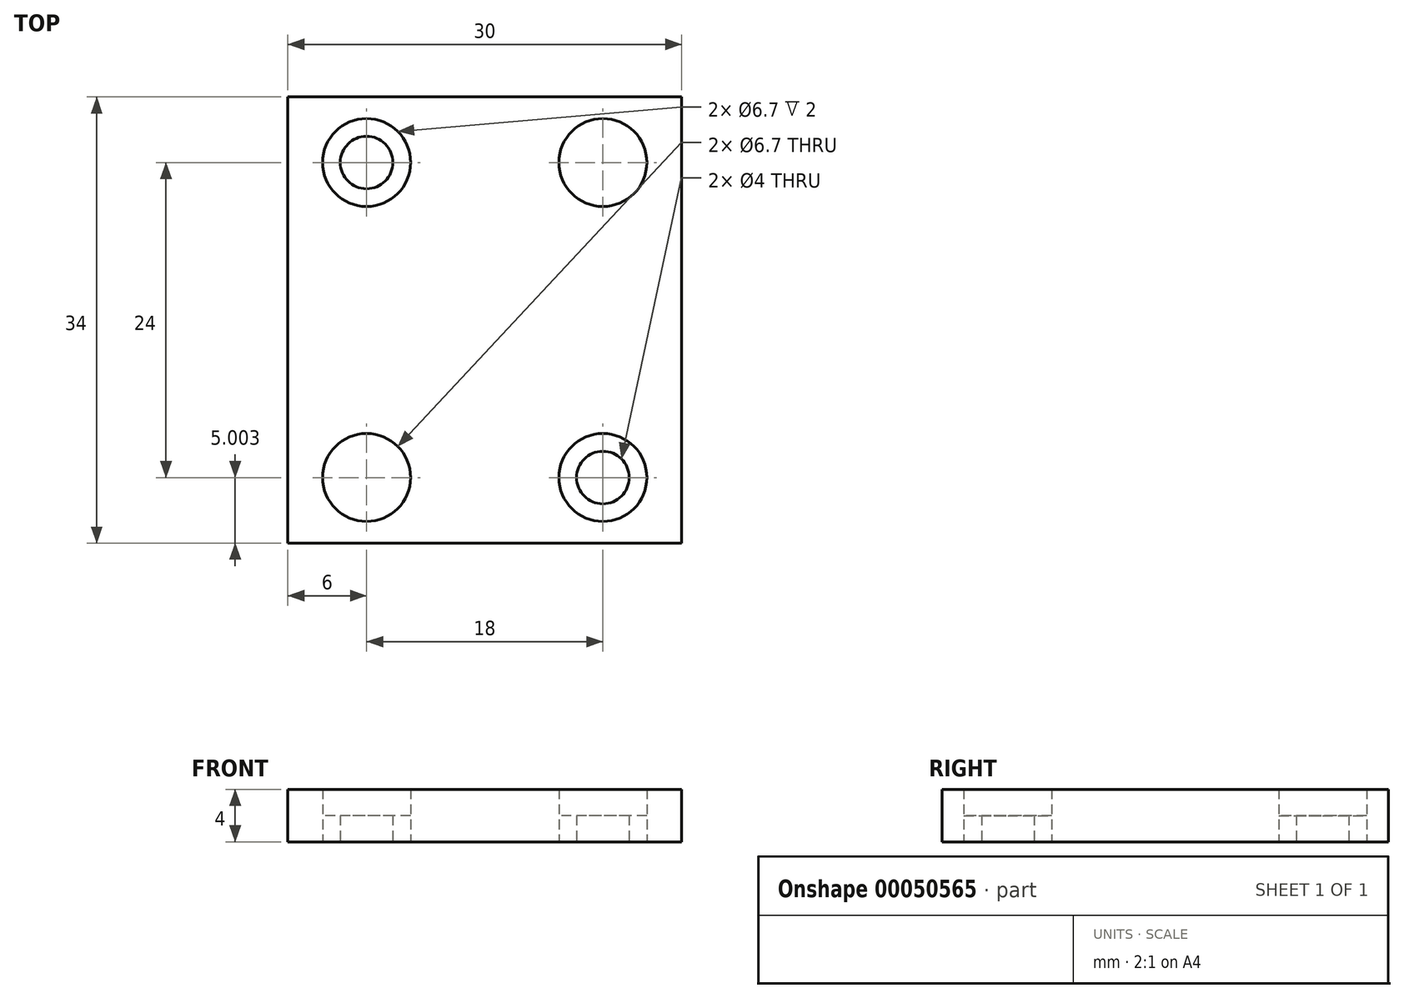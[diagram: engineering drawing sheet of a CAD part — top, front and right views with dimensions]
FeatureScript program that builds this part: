
annotation { "Feature Type Name" : "Feature", "Feature Type Description" : "" }
export const myFeature = defineFeature(function(context is Context, id is Id, definition is map)
    precondition{}
    {
        {
            var Q0;
            Q0=qCreatedBy(makeId("Top.planeOp"),FACE);
            var sketch = newSketch(context, id + "F0", { "sketchPlane" : qUnion([Q0])});
            skLineSegment(sketch, "E0.bottom", {"start": v(-13, 20.28) * mm, "end": v(17, 20.28) * mm});
            skLineSegment(sketch, "E0.top", {"start": v(-13, -13.72) * mm, "end": v(17, -13.72) * mm});
            skLineSegment(sketch, "E0.left", {"start": v(-13, 20.28) * mm, "end": v(-13, -13.72) * mm});
            skLineSegment(sketch, "E0.right", {"start": v(17, 20.28) * mm, "end": v(17, -13.72) * mm});
            skLineSegment(sketch, "E1.0", {"start": v(-7, 20.28) * mm, "end": v(-7, -13.72) * mm, "construction": true});
            skLineSegment(sketch, "E2.0", {"start": v(11, 20.28) * mm, "end": v(11, -13.72) * mm, "construction": true});
            skLineSegment(sketch, "E3.0", {"start": v(-13, 15.28) * mm, "end": v(17, 15.28) * mm, "construction": true});
            skLineSegment(sketch, "E4.0", {"start": v(-13, -8.72) * mm, "end": v(17, -8.72) * mm, "construction": true});
            skCircle(sketch, "E5", {"center": v(-7, 15.28) * mm, "radius": 2 * mm});
            skCircle(sketch, "E6", {"center": v(-7, 15.28) * mm, "radius": 3.35 * mm});
            skLineSegment(sketch, "E7", {"start": v(2, 20.28) * mm, "end": v(2, -13.72) * mm, "construction": true});
            skLineSegment(sketch, "E8", {"start": v(17, 3.28) * mm, "end": v(-13, 3.28) * mm, "construction": true});
            skCircle(sketch, "E9.MirrorC", {"center": v(11, 15.28) * mm, "radius": 3.35 * mm});
            skCircle(sketch, "E10.MirrorC", {"center": v(11, 15.28) * mm, "radius": 2 * mm});
            skCircle(sketch, "E11.MirrorC", {"center": v(11, -8.72) * mm, "radius": 3.35 * mm});
            skCircle(sketch, "E12.MirrorC", {"center": v(11, -8.72) * mm, "radius": 2 * mm});
            skCircle(sketch, "E13.MirrorC", {"center": v(-7, -8.72) * mm, "radius": 3.35 * mm});
            skCircle(sketch, "E14.MirrorC", {"center": v(-7, -8.72) * mm, "radius": 2 * mm});
            skSolve(sketch);
        }
        {
            var Q0;
            Q0=makeQuery(id+"F0.imprint","IMPRINT",FACE,{"disambiguationData":[TD([[makeQuery(id+"F0.imprint","IMPRINT",EDGE,{"derivedFrom":sQuery(id+"F0.wireOp",EDGE,"E0.bottom")}),-1.0]])]});
            extrude(context, id + "F1", {"entities" : qUnion([Q0]), "depth" : 4 * mm});
        }
        {
            var Q0;
            Q0=makeQuery(id+"F0.imprint","IMPRINT",FACE,{"disambiguationData":[TD([[makeQuery(id+"F0.imprint","IMPRINT",EDGE,{"derivedFrom":sQuery(id+"F0.wireOp",EDGE,"E5")}),-1.0]])]});
            var Q1;
            Q1=makeQuery(id+"F0.imprint","IMPRINT",FACE,{"disambiguationData":[TD([[makeQuery(id+"F0.imprint","IMPRINT",EDGE,{"derivedFrom":sQuery(id+"F0.wireOp",EDGE,"E9.MirrorC")}),-1.0]])]});
            var Q2;
            Q2=makeQuery(id+"F0.imprint","IMPRINT",FACE,{"disambiguationData":[TD([[makeQuery(id+"F0.imprint","IMPRINT",EDGE,{"derivedFrom":sQuery(id+"F0.wireOp",EDGE,"E11.MirrorC")}),1.0]])]});
            var Q3;
            Q3=makeQuery(id+"F0.imprint","IMPRINT",FACE,{"disambiguationData":[TD([[makeQuery(id+"F0.imprint","IMPRINT",EDGE,{"derivedFrom":sQuery(id+"F0.wireOp",EDGE,"E13.MirrorC")}),-1.0]])]});
            extrude(context, id + "F2", {"entities" : qUnion([Q0, Q1, Q2, Q3]), "operationType" : NewBodyOperationType.ADD, "depth" : 2 * mm});
        }
        {
            var Q0;
            Q0=makeQuery(id+"F1.opExtrude","SWEPT_FACE",FACE,{"disambiguationData":[OSD([sQuery(id+"F0.wireOp",EDGE,"E0.right")])]});
            var sketch = newSketch(context, id + "F3", { "sketchPlane" : qUnion([Q0])});
            skLineSegment(sketch, "E15.0.0", {"start": v(-13.72, 0) * mm, "end": v(20.28, 0) * mm});
            skLineSegment(sketch, "E15.0.1", {"start": v(20.28, 0) * mm, "end": v(20.28, 4) * mm});
            skLineSegment(sketch, "E15.0.2", {"start": v(20.28, 4) * mm, "end": v(-13.72, 4) * mm});
            skLineSegment(sketch, "E15.0.3", {"start": v(-13.72, 4) * mm, "end": v(-13.72, 0) * mm});
            skLineSegment(sketch, "E16", {"start": v(3.28, 4) * mm, "end": v(3.28, 0) * mm, "construction": true});
            skLineSegment(sketch, "E17.0", {"start": v(-0.72, 4) * mm, "end": v(-0.72, 0) * mm});
            skLineSegment(sketch, "E18.0", {"start": v(7.28, 4) * mm, "end": v(7.28, 0) * mm});
            skSolve(sketch);
        }
    });
